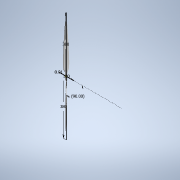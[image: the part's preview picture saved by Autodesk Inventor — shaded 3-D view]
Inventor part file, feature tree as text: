
AUTODESK INVENTOR PART (.ipt)
format: ipt  version: 2022 (Build 260153000, 153)  size: 1,512,448 bytes
history: native  units: mm
features: sketch x8, sweep x2, extrude x1
ambient origin geometry x8: Origin, YZ Plane, XZ Plane, XY Plane, X Axis, Y Axis, Z Axis, Center Point
bodies: Solid1 (feature_tree), Solid2 (feature_tree)
feature tree (11):
  sketch  "Sketch1"  dims[d1=0.0mm d2=380.0mm]
  sketch  "Sketch2"  dims[d3=100.0mm d4=0.01mm]
  sketch  "3D Sketch1"
  sketch  "Sketch3"  dims[d5=0.0mm d6=0.0mm d7=330.0mm]
  sweep  "Sweep1"
  sweep  "Sweep2"
  sketch  "Sketch5"  dims[d9=0.0mm d10=0.0mm]
  extrude  "Extrusion1"  Depth=330.0mm
  sketch  "Sketch4"  dims[d8=90.0deg]
  sketch  "3D Sketch2"
  sketch  "Sketch6"  dims[d11=380.0mm d12=90.0deg d13=2000.0mm d14=0.0mm]
